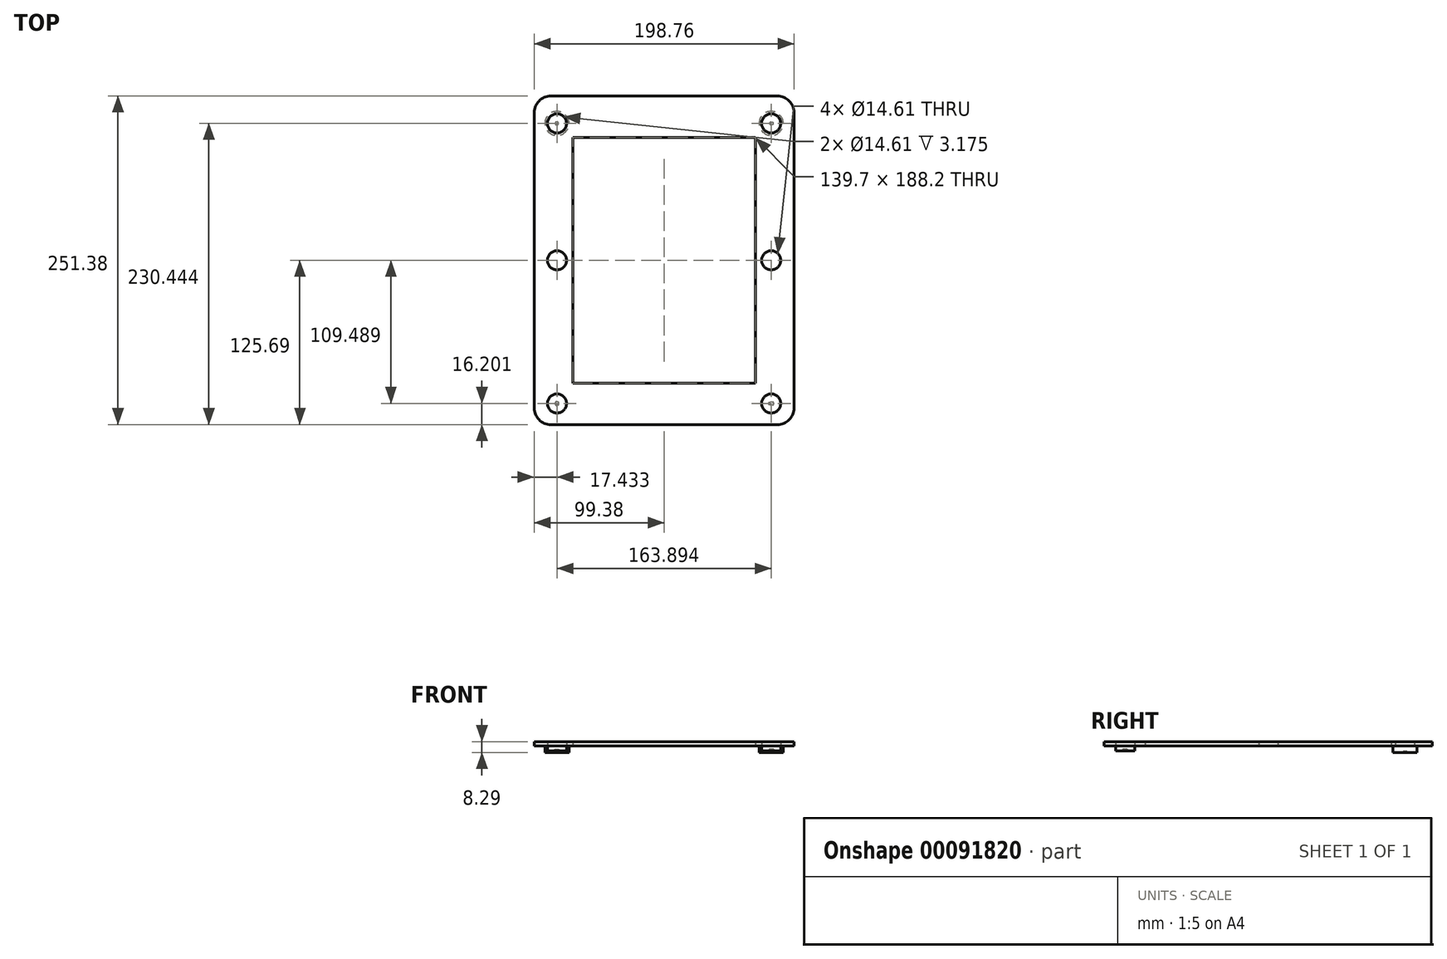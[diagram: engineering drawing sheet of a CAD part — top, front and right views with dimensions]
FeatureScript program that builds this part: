
annotation { "Feature Type Name" : "Feature", "Feature Type Description" : "" }
export const myFeature = defineFeature(function(context is Context, id is Id, definition is map)
    precondition{}
    {
        {
            var Q0;
            Q0=qCreatedBy(makeId("Top.planeOp"),FACE);
            var sketch = newSketch(context, id + "F0", { "sketchPlane" : qUnion([Q0])});
            skLineSegment(sketch, "E0.bottom", {"start": v(-86.68, -125.7) * mm, "end": v(86.68, -125.7) * mm});
            skLineSegment(sketch, "E0.top", {"start": v(-86.68, 125.7) * mm, "end": v(86.68, 125.7) * mm});
            skLineSegment(sketch, "E0.left", {"start": v(-99.38, -113) * mm, "end": v(-99.38, 113) * mm});
            skLineSegment(sketch, "E0.right", {"start": v(99.38, -113) * mm, "end": v(99.38, 113) * mm});
            skPoint(sketch, "E0.middle", {"position": v(0, 0) * mm});
            skLineSegment(sketch, "E1.bottom", {"start": v(-69.85, 94.1) * mm, "end": v(69.85, 94.1) * mm});
            skLineSegment(sketch, "E1.top", {"start": v(-69.85, -94.1) * mm, "end": v(69.85, -94.1) * mm});
            skLineSegment(sketch, "E1.left", {"start": v(-69.85, 94.1) * mm, "end": v(-69.85, -94.1) * mm});
            skLineSegment(sketch, "E1.right", {"start": v(69.85, 94.1) * mm, "end": v(69.85, -94.1) * mm});
            skCircle(sketch, "E2", {"center": v(-81.95, 0) * mm, "radius": 7.3 * mm});
            skCircle(sketch, "E3", {"center": v(-81.95, 104.75) * mm, "radius": 7.3 * mm});
            skCircle(sketch, "E4", {"center": v(-81.95, -109.49) * mm, "radius": 7.3 * mm});
            skCircle(sketch, "E5.MirrorC", {"center": v(81.95, 104.75) * mm, "radius": 7.3 * mm});
            skCircle(sketch, "E6.MirrorC", {"center": v(81.95, 0) * mm, "radius": 7.3 * mm});
            skCircle(sketch, "E7.MirrorC", {"center": v(81.95, -109.49) * mm, "radius": 7.3 * mm});
            skPoint(sketch, "E8.visualSharp", {"position": v(-99.38, 125.7) * mm});
            skArc(sketch, "E8.filletArc", {"start": v(-86.68, 125.7) * mm, "mid": v(-95.66, 121.97) * mm, "end": v(-99.38, 113) * mm});
            skPoint(sketch, "E9.visualSharp", {"position": v(99.38, 125.7) * mm});
            skArc(sketch, "E9.filletArc", {"start": v(99.38, 113) * mm, "mid": v(95.66, 121.97) * mm, "end": v(86.68, 125.7) * mm});
            skPoint(sketch, "E10.visualSharp", {"position": v(99.38, -125.7) * mm});
            skArc(sketch, "E10.filletArc", {"start": v(86.68, -125.7) * mm, "mid": v(95.66, -121.97) * mm, "end": v(99.38, -113) * mm});
            skPoint(sketch, "E11.visualSharp", {"position": v(-99.38, -125.7) * mm});
            skArc(sketch, "E11.filletArc", {"start": v(-99.38, -113) * mm, "mid": v(-95.66, -121.97) * mm, "end": v(-86.68, -125.7) * mm});
            skSolve(sketch);
        }
        {
            var Q0;
            Q0=makeQuery(id+"F0.imprint","IMPRINT",FACE,{"disambiguationData":[TD([[makeQuery(id+"F0.imprint","IMPRINT",EDGE,{"derivedFrom":sQuery(id+"F0.wireOp",EDGE,"E0.bottom")}),1.0]])]});
            extrude(context, id + "F1", {"entities" : qUnion([Q0]), "depth" : 3.17 * mm});
        }
        {
            var Q0;
            Q0=makeQuery(id+"F1.opExtrude","CAP_FACE",FACE,{"disambiguationData":[OSD([sQuery(id+"F0.wireOp",EDGE,"E0.bottom"),sQuery(id+"F0.wireOp",EDGE,"E0.top"),sQuery(id+"F0.wireOp",EDGE,"E0.left"),sQuery(id+"F0.wireOp",EDGE,"E0.right"),sQuery(id+"F0.wireOp",EDGE,"E1.bottom"),sQuery(id+"F0.wireOp",EDGE,"E1.top"),sQuery(id+"F0.wireOp",EDGE,"E1.left"),sQuery(id+"F0.wireOp",EDGE,"E1.right"),sQuery(id+"F0.wireOp",EDGE,"E2"),sQuery(id+"F0.wireOp",EDGE,"E3"),sQuery(id+"F0.wireOp",EDGE,"E4"),sQuery(id+"F0.wireOp",EDGE,"E5.MirrorC"),sQuery(id+"F0.wireOp",EDGE,"E6.MirrorC"),sQuery(id+"F0.wireOp",EDGE,"E7.MirrorC"),sQuery(id+"F0.wireOp",EDGE,"E8.filletArc"),sQuery(id+"F0.wireOp",EDGE,"E9.filletArc"),sQuery(id+"F0.wireOp",EDGE,"E10.filletArc"),sQuery(id+"F0.wireOp",EDGE,"E11.filletArc")])],"isStart":true});
            var sketch = newSketch(context, id + "F2", { "sketchPlane" : qUnion([Q0])});
            skCircle(sketch, "E12", {"center": v(-81.95, 109.49) * mm, "radius": 10.88 * mm});
            skSolve(sketch);
        }
        {
            var Q0;
            Q0=makeQuery(id+"F2.imprint","IMPRINT",FACE,{"disambiguationData":[TD([[makeQuery(id+"F2.imprint","IMPRINT",EDGE,{"derivedFrom":makeQuery(id+"F1.opExtrude","CAP_EDGE",EDGE,{"disambiguationData":[OSD([sQuery(id+"F0.wireOp",EDGE,"E4")])],"isStart":true})}),-1.0]])]});
            extrude(context, id + "F3", {"entities" : qUnion([Q0]), "depth" : 3.92 * mm});
        }
        {
            var Q0;
            Q0=makeQuery(id+"F3.opExtrude","CAP_FACE",FACE,{"disambiguationData":[OSD([sQuery(id+"F0.wireOp",EDGE,"E4")])],"isStart":false});
            var sketch = newSketch(context, id + "F4", { "sketchPlane" : qUnion([Q0])});
            skCircle(sketch, "E13.cCircle", {"center": v(-81.95, 109.49) * mm, "radius": 1.43 * mm, "construction": true});
            skLineSegment(sketch, "E13.0", {"start": v(-80.52, 110.53) * mm, "end": v(-80.52, 108.45) * mm});
            skLineSegment(sketch, "E13.1", {"start": v(-80.52, 108.45) * mm, "end": v(-82.5, 107.8) * mm});
            skLineSegment(sketch, "E13.2", {"start": v(-82.5, 107.8) * mm, "end": v(-83.72, 109.49) * mm});
            skLineSegment(sketch, "E13.3", {"start": v(-83.72, 109.49) * mm, "end": v(-82.5, 111.17) * mm});
            skLineSegment(sketch, "E13.4", {"start": v(-82.5, 111.17) * mm, "end": v(-80.52, 110.53) * mm});
            skPoint(sketch, "E13.0.midPoint", {"position": v(-80.52, 109.49) * mm});
            skSolve(sketch);
        }
        {
            var Q0;
            Q0=makeQuery(id+"F4.imprint","IMPRINT",FACE,{"disambiguationData":[TD([[makeQuery(id+"F4.imprint","IMPRINT",EDGE,{"derivedFrom":sQuery(id+"F4.wireOp",EDGE,"E13.0")}),-1.0]])]});
            extrude(context, id + "F5", {"entities" : qUnion([Q0]), "operationType" : NewBodyOperationType.REMOVE, "oppositeDirection" : true, "depth" : 1.27 * mm});
        }
        {
            var Q0;
            Q0=makeQuery(id+"F1.opExtrude","CAP_FACE",FACE,{"disambiguationData":[OSD([sQuery(id+"F0.wireOp",EDGE,"E0.bottom"),sQuery(id+"F0.wireOp",EDGE,"E0.top"),sQuery(id+"F0.wireOp",EDGE,"E0.left"),sQuery(id+"F0.wireOp",EDGE,"E0.right"),sQuery(id+"F0.wireOp",EDGE,"E1.bottom"),sQuery(id+"F0.wireOp",EDGE,"E1.top"),sQuery(id+"F0.wireOp",EDGE,"E1.left"),sQuery(id+"F0.wireOp",EDGE,"E1.right"),sQuery(id+"F0.wireOp",EDGE,"E2"),sQuery(id+"F0.wireOp",EDGE,"E3"),sQuery(id+"F0.wireOp",EDGE,"E4"),sQuery(id+"F0.wireOp",EDGE,"E5.MirrorC"),sQuery(id+"F0.wireOp",EDGE,"E6.MirrorC"),sQuery(id+"F0.wireOp",EDGE,"E7.MirrorC"),sQuery(id+"F0.wireOp",EDGE,"E8.filletArc"),sQuery(id+"F0.wireOp",EDGE,"E9.filletArc"),sQuery(id+"F0.wireOp",EDGE,"E10.filletArc"),sQuery(id+"F0.wireOp",EDGE,"E11.filletArc")])],"isStart":true});
            var sketch = newSketch(context, id + "F6", { "sketchPlane" : qUnion([Q0])});
            skCircle(sketch, "E14", {"center": v(-81.95, -104.75) * mm, "radius": 9.22 * mm});
            skSolve(sketch);
        }
        {
            var Q0;
            Q0 = qSketchRegion(id + "F6", true);
            extrude(context, id + "F7", {"entities" : qUnion([Q0]), "operationType" : NewBodyOperationType.ADD, "depth" : 5.1 * mm});
        }
        {
            var Q0;
            Q0=makeQuery(id+"F7.opExtrude","CAP_FACE",FACE,{"disambiguationData":[OSD([sQuery(id+"F6.wireOp",EDGE,"E14")])],"isStart":false});
            var sketch = newSketch(context, id + "F8", { "sketchPlane" : qUnion([Q0])});
            skCircle(sketch, "E15.cCircle", {"center": v(-81.95, -104.75) * mm, "radius": 1.17 * mm, "construction": true});
            skLineSegment(sketch, "E15.0", {"start": v(-81.52, -103.38) * mm, "end": v(-80.5, -104.73) * mm});
            skLineSegment(sketch, "E15.1", {"start": v(-80.5, -104.73) * mm, "end": v(-81.48, -106.12) * mm});
            skLineSegment(sketch, "E15.2", {"start": v(-81.48, -106.12) * mm, "end": v(-83.1, -105.62) * mm});
            skLineSegment(sketch, "E15.3", {"start": v(-83.1, -105.62) * mm, "end": v(-83.13, -103.92) * mm});
            skLineSegment(sketch, "E15.4", {"start": v(-83.13, -103.92) * mm, "end": v(-81.52, -103.38) * mm});
            skPoint(sketch, "E15.0.midPoint", {"position": v(-81.01, -104.06) * mm});
            skSolve(sketch);
        }
        {
            var Q0;
            Q0 = qSketchRegion(id + "F8", true);
            extrude(context, id + "F9", {"entities" : qUnion([Q0]), "operationType" : NewBodyOperationType.REMOVE, "oppositeDirection" : true, "depth" : 0.85 * mm});
        }
        {
            var Q0;
            Q0=makeQuery(id+"F3.opExtrude","SWEPT_BODY",BODY,{"disambiguationData":[OSD([sQuery(id+"F0.wireOp",EDGE,"E4")])]});
            var Q1;
            Q1=makeQuery(id+"F1.opExtrude","SWEPT_BODY",BODY,{"disambiguationData":[OSD([sQuery(id+"F0.wireOp",EDGE,"E0.bottom"),sQuery(id+"F0.wireOp",EDGE,"E0.top"),sQuery(id+"F0.wireOp",EDGE,"E0.left"),sQuery(id+"F0.wireOp",EDGE,"E0.right"),sQuery(id+"F0.wireOp",EDGE,"E1.bottom"),sQuery(id+"F0.wireOp",EDGE,"E1.top"),sQuery(id+"F0.wireOp",EDGE,"E1.left"),sQuery(id+"F0.wireOp",EDGE,"E1.right"),sQuery(id+"F0.wireOp",EDGE,"E2"),sQuery(id+"F0.wireOp",EDGE,"E3"),sQuery(id+"F0.wireOp",EDGE,"E4"),sQuery(id+"F0.wireOp",EDGE,"E5.MirrorC"),sQuery(id+"F0.wireOp",EDGE,"E6.MirrorC"),sQuery(id+"F0.wireOp",EDGE,"E7.MirrorC"),sQuery(id+"F0.wireOp",EDGE,"E8.filletArc"),sQuery(id+"F0.wireOp",EDGE,"E9.filletArc"),sQuery(id+"F0.wireOp",EDGE,"E10.filletArc"),sQuery(id+"F0.wireOp",EDGE,"E11.filletArc")])]});
            var Q2;
            Q2=qCreatedBy(makeId("Right.planeOp"),FACE);
            mirror(context, id + "F10", {"operationType" : NewBodyOperationType.ADD, "entities" : qUnion([Q0, Q1]), "mirrorPlane" : qUnion([Q2])});
        }
    });
